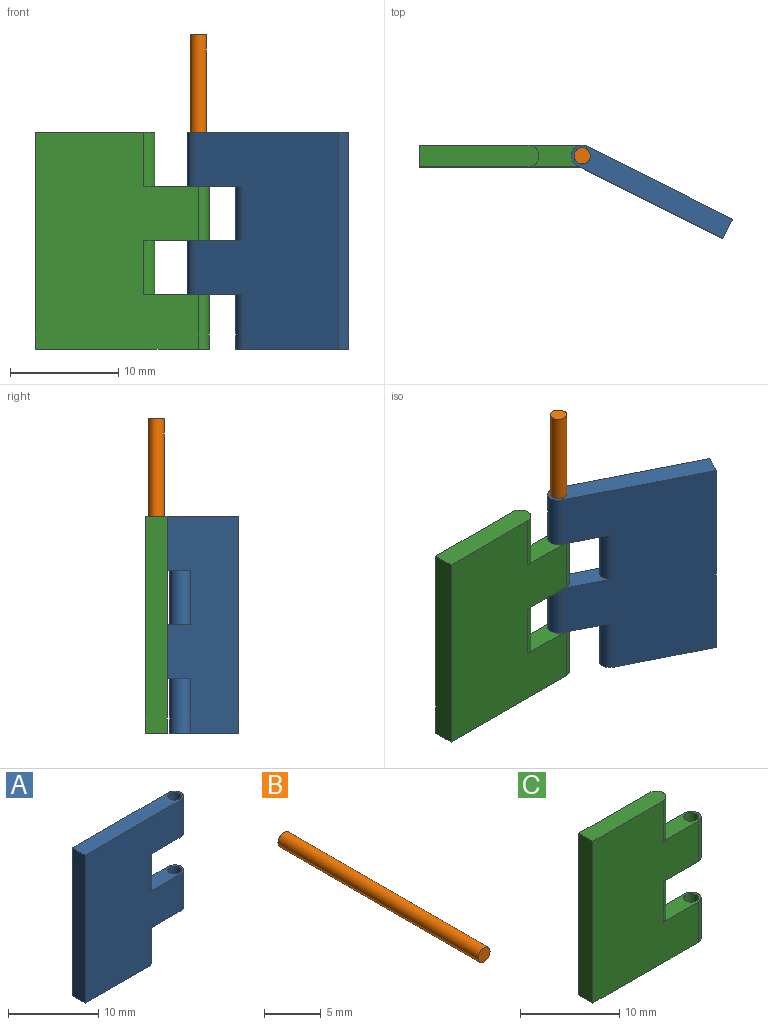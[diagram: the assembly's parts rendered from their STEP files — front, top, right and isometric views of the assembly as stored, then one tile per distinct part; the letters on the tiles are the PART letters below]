
ASSEMBLY  parts=3 mates=2
PART A: 14 faces, bbox 16x2x20 mm
  f0: plane 20x2mm, normal (-1,0,0), area 40mm2, adj f1,f5,f6,f7
  f1: plane 11.01x2mm, normal (0,0,-1), area 21.6mm2, adj f0,f6,f7,f11
  f2: plane 6x2mm, normal (0,0,-1), area 8.2mm2, adj f6,f7,f8,f11,f13
  f3: plane 6x2mm, normal (0,0,1), area 8.2mm2, adj f6,f7,f8,f10,f13
  f4: plane 6x2mm, normal (0,0,-1), area 8.2mm2, adj f6,f7,f9,f10,f12
  f5: plane 16.01x2mm, normal (0,0,1), area 29.8mm2, adj f0,f6,f7,f9,f12
  f6: plane 20x15.01mm, normal (0,-1,0), area 250.2mm2, adj f0,f1,f2,f3,f4,f5,f8,f9
  f7: plane 20x15.01mm, normal (0,1,0), area 250.2mm2, adj f0,f1,f2,f3,f4,f5,f8,f9
  f8: cylinder r=1mm len=5mm, axis (0,0,-1), area 15.7mm2, adj f2,f3,f6,f7
  f9: cylinder r=1mm len=5mm, axis (0,0,-1), area 15.7mm2, adj f4,f5,f6,f7
  f10: cylinder r=1mm len=5mm, axis (0,0,-1), area 15.7mm2, adj f3,f4,f6,f7
  f11: cylinder r=1mm len=5mm, axis (0,0,-1), area 15.7mm2, adj f1,f2,f6,f7
  f12: cylinder r=0.75mm len=5mm, axis (0,0,1), area 23.6mm2, adj f4,f5
  f13: cylinder r=0.75mm len=5mm, axis (0,0,1), area 23.6mm2, adj f2,f3
PART B: 3 faces, bbox 1.5x25x1.5 mm
  f0: cylinder r=0.75mm len=25mm, axis (0,1,0), area 117.8mm2, adj f1,f2
  f1: plane 1.5x1.5mm, normal (0,-1,0), area 1.8mm2, adj f0
  f2: plane 1.5x1.5mm, normal (0,1,0), area 1.8mm2, adj f0
PART C: 14 faces, bbox 16x2x20 mm
  f0: plane 6x2mm, normal (0,0,1), area 8.2mm2, adj f6,f7,f10,f11,f12
  f1: plane 6x2mm, normal (0,0,-1), area 8.2mm2, adj f6,f7,f9,f10,f13
  f2: plane 6x2mm, normal (0,0,1), area 8.2mm2, adj f6,f7,f8,f9,f13
  f3: plane 11.01x2mm, normal (0,0,1), area 21.6mm2, adj f4,f6,f7,f8
  f4: plane 20x2mm, normal (-1,0,0), area 40mm2, adj f3,f5,f6,f7
  f5: plane 16.01x2mm, normal (0,0,-1), area 29.8mm2, adj f4,f6,f7,f11,f12
  f6: plane 20x15.01mm, normal (0,-1,0), area 250.2mm2, adj f0,f1,f2,f3,f4,f5,f8,f9
  f7: plane 20x15.01mm, normal (0,1,0), area 250.2mm2, adj f0,f1,f2,f3,f4,f5,f8,f9
  f8: cylinder r=1mm len=5mm, axis (0,0,-1), area 15.7mm2, adj f2,f3,f6,f7
  f9: cylinder r=1mm len=5mm, axis (0,0,-1), area 15.7mm2, adj f1,f2,f6,f7
  f10: cylinder r=1mm len=5mm, axis (0,0,-1), area 15.7mm2, adj f0,f1,f6,f7
  f11: cylinder r=1mm len=5mm, axis (0,0,-1), area 15.7mm2, adj f0,f5,f6,f7
  f12: cylinder r=0.75mm len=5mm, axis (0,0,-1), area 23.6mm2, adj f0,f5
  f13: cylinder r=0.75mm len=5mm, axis (0,0,-1), area 23.6mm2, adj f1,f2
PLACE A rot(axis=(0,0,1),153.4deg) t=(-88.15,24.67,-11.76)mm
PLACE B rot(axis=(0.75,0.47,0.47),106deg) t=(-64.25,30.21,21.42)mm
PLACE C t=(-19.43,10.43,-11.76)mm fixed
MATE slider B.f0 <-> A.f12  axis (0,0,1) through (-55.47,9.43,21.42)mm
MATE revolute A.f9 <-> C.f11  axis (0,0,-1) through (-55.47,9.43,7.45)mm
